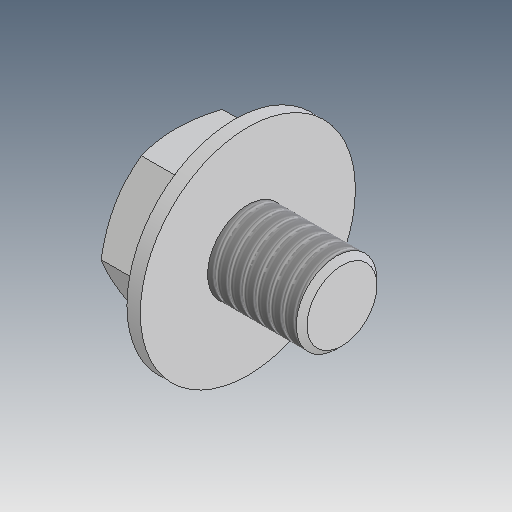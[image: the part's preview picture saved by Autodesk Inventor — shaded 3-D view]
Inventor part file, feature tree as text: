
AUTODESK INVENTOR PART (.ipt)
format: ipt  version: 2017 (Build 210142000, 142)  size: 157,184 bytes
history: native  units: in
note: dims shown in document units (in); Inventor stores cm internally (conversion verified against a paired STEP export)
features: sketch x3, extrude x2, revolve x1, chamfer x1, thread x1
ambient origin geometry x8: Origin, YZ Plane, XZ Plane, XY Plane, X Axis, Y Axis, Z Axis, Center Point
bodies: Solid1 (feature_tree)
feature tree (8):
  revolve  "Revolution1"  Angle=30.0deg
  extrude  "Extrusion15"  Depth=0.0197in
  chamfer  "Chamfer5"  Angle=90.0deg  [1 undecoded]
  thread  "Thread7"  [1 undecoded]
  extrude  "Extrusion18"  Depth=0.0886in
  sketch  "Sketch15"  dims[d21=0.7874in d83=30.0deg]
  sketch  "Sketch16"  dims[d84=0.0591in d86=0.0197in]
  sketch  "Sketch19"  dims[d87=0.1181in d92=90.0deg d105=0.1969in d106=0.0in d116=0.0886in d117=0.1575in d118=0.0079in d119=0.0787in d120=45.0deg d128=0.1181in d129=0.3937in d130=0.0in d131=0.315in d132=0.0197in d133=0.0in]
note: 2 required parameter values undecoded (feature->parameter linkage not recoverable at this tier; creation-order binding heuristic only, values carry confidence <= 0.55)
